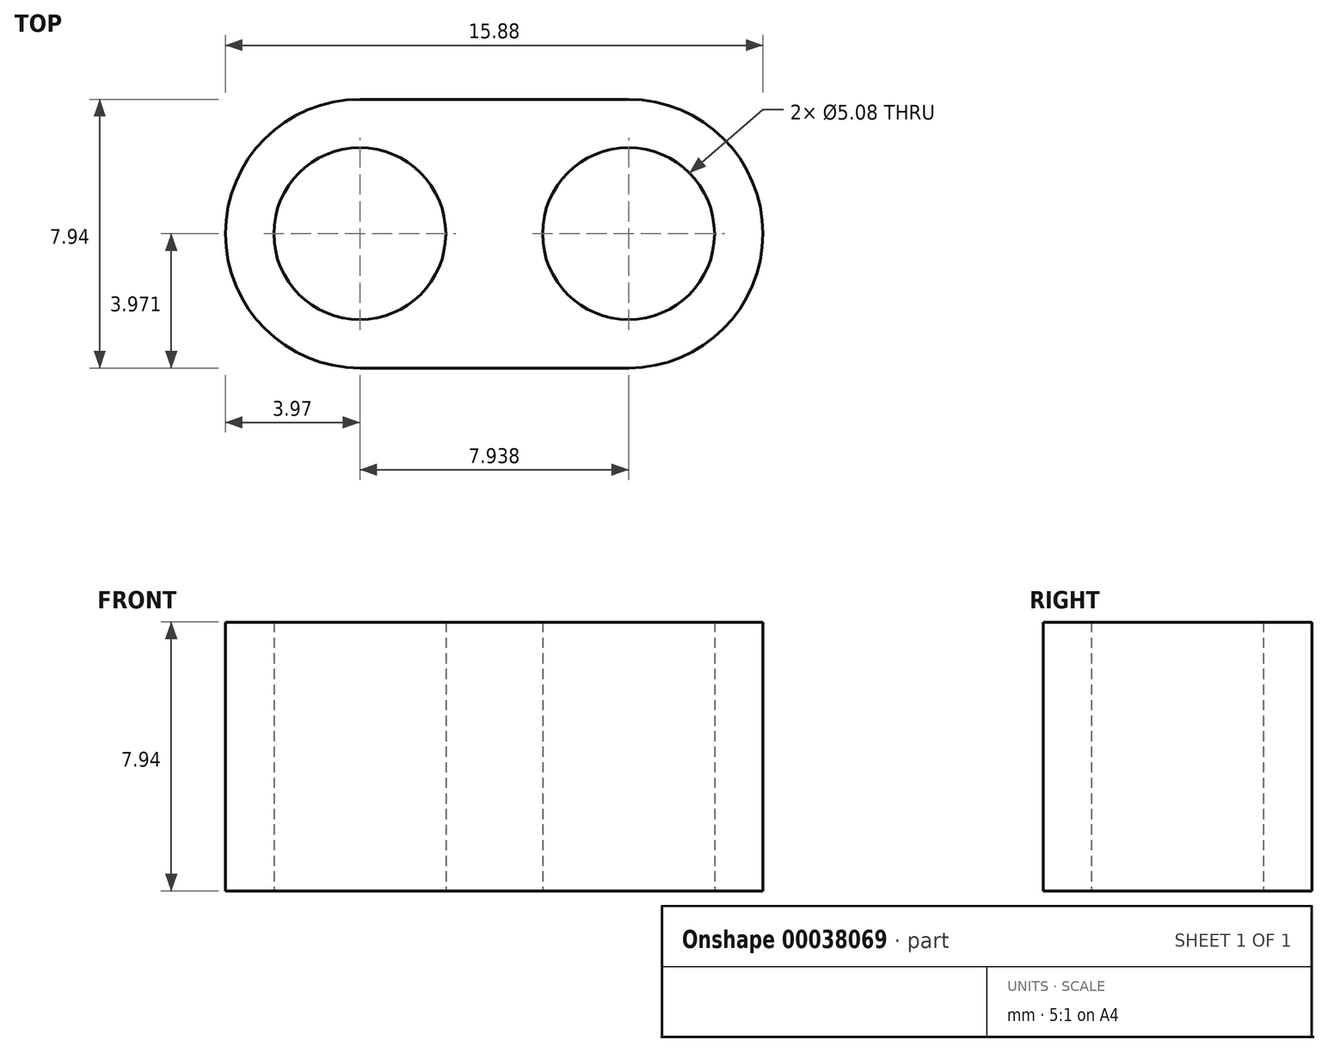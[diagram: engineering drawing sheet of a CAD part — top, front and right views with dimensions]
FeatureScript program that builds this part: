
annotation { "Feature Type Name" : "Feature", "Feature Type Description" : "" }
export const myFeature = defineFeature(function(context is Context, id is Id, definition is map)
    precondition{}
    {
        {
            var Q0;
            Q0=qCreatedBy(makeId("Top.planeOp"),FACE);
            var sketch = newSketch(context, id + "F0", { "sketchPlane" : qUnion([Q0])});
            skLineSegment(sketch, "E0.bottom", {"start": v(0, 0) * mm, "end": v(7.94, 0) * mm});
            skLineSegment(sketch, "E0.top", {"start": v(0, -7.94) * mm, "end": v(7.94, -7.94) * mm});
            skLineSegment(sketch, "E0.left", {"start": v(0, 0) * mm, "end": v(0, -7.94) * mm, "construction": true});
            skLineSegment(sketch, "E0.right", {"start": v(7.94, 0) * mm, "end": v(7.94, -7.94) * mm, "construction": true});
            skArc(sketch, "E1", {"start": v(0, 0) * mm, "mid": v(-3.97, -3.97) * mm, "end": v(0, -7.94) * mm});
            skArc(sketch, "E2", {"start": v(7.94, -7.94) * mm, "mid": v(11.9, -3.97) * mm, "end": v(7.94, 0) * mm});
            skCircle(sketch, "E3", {"center": v(0, -3.97) * mm, "radius": 2.54 * mm});
            skCircle(sketch, "E4", {"center": v(7.94, -3.97) * mm, "radius": 2.54 * mm});
            skSolve(sketch);
        }
        {
            var Q0;
            Q0 = qSketchRegion(id + "F0", true);
            extrude(context, id + "F1", {"entities" : qUnion([Q0]), "depth" : 7.94 * mm});
        }
    });
